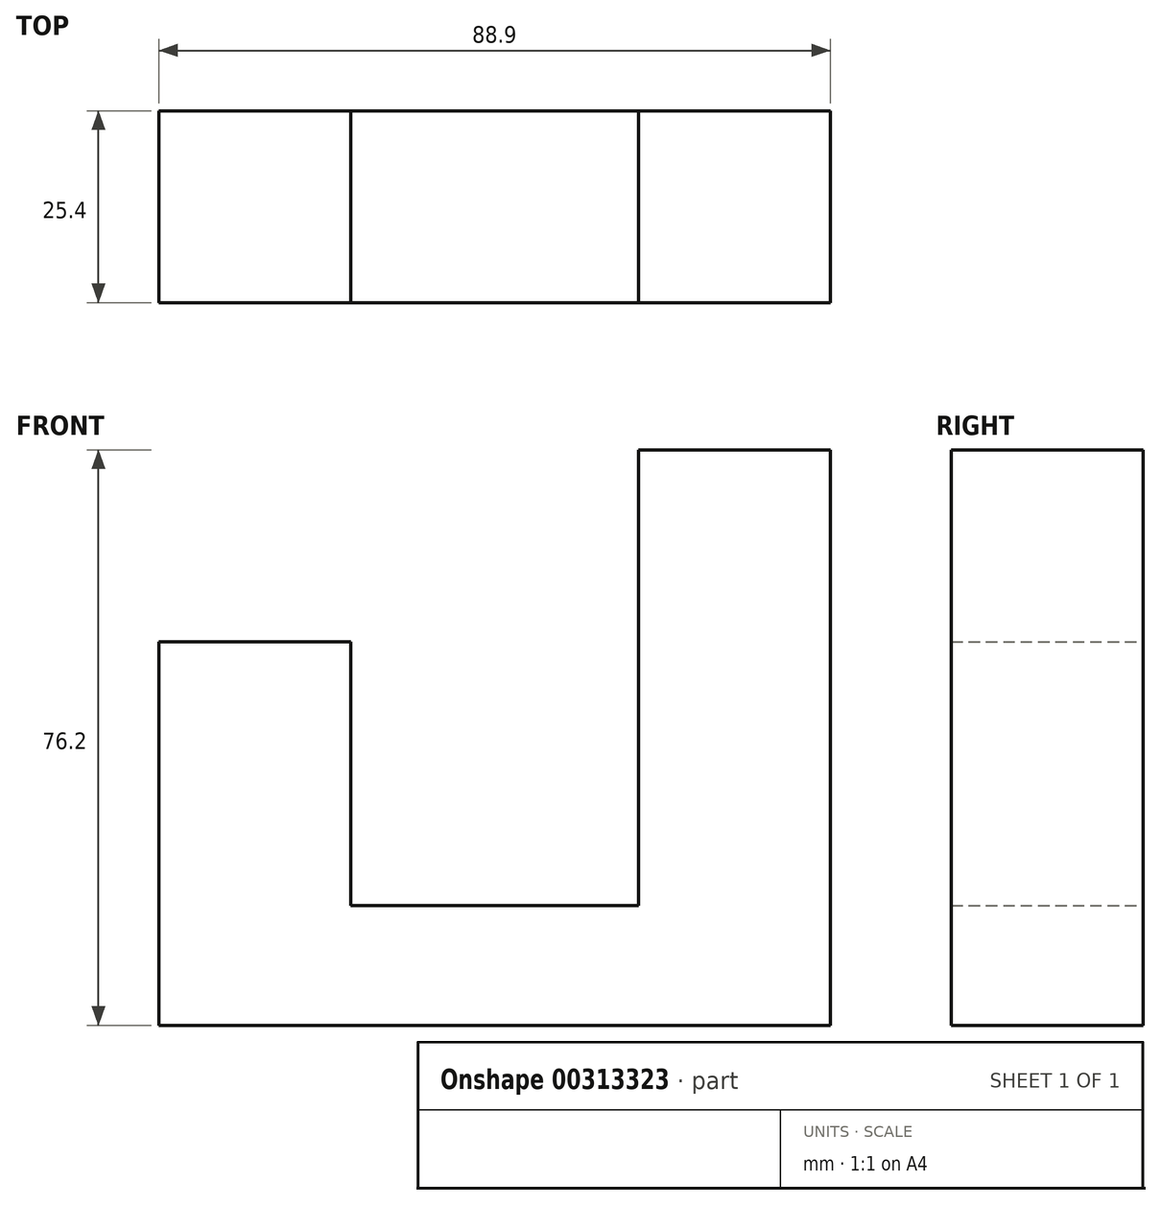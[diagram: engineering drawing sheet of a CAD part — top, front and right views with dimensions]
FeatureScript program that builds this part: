
annotation { "Feature Type Name" : "Feature", "Feature Type Description" : "" }
export const myFeature = defineFeature(function(context is Context, id is Id, definition is map)
    precondition{}
    {
        {
            var Q0;
            Q0=qCreatedBy(makeId("Front.planeOp"),FACE);
            var sketch = newSketch(context, id + "F0", { "sketchPlane" : qUnion([Q0])});
            skLineSegment(sketch, "E0", {"start": v(-58.85, 21.4) * mm, "end": v(-58.85, -29.4) * mm});
            skLineSegment(sketch, "E1", {"start": v(-58.85, -29.4) * mm, "end": v(30.05, -29.4) * mm});
            skLineSegment(sketch, "E2", {"start": v(30.05, -29.4) * mm, "end": v(30.05, 46.8) * mm});
            skLineSegment(sketch, "E3", {"start": v(30.05, 46.8) * mm, "end": v(4.65, 46.8) * mm});
            skLineSegment(sketch, "E4", {"start": v(4.65, 46.8) * mm, "end": v(4.65, -13.57) * mm});
            skLineSegment(sketch, "E5", {"start": v(4.65, -13.57) * mm, "end": v(-33.45, -13.57) * mm});
            skLineSegment(sketch, "E6", {"start": v(-33.45, -13.57) * mm, "end": v(-33.45, 21.4) * mm});
            skLineSegment(sketch, "E7", {"start": v(-58.85, 21.4) * mm, "end": v(-33.45, 21.4) * mm});
            skSolve(sketch);
        }
        {
            var Q0;
            Q0=makeQuery(id+"F0.imprint","IMPRINT",FACE,{"disambiguationData":[TD([[makeQuery(id+"F0.imprint","IMPRINT",EDGE,{"derivedFrom":sQuery(id+"F0.wireOp",EDGE,"E0")}),1.0]])]});
            extrude(context, id + "F1", {"entities" : qUnion([Q0]), "depth" : 25.4 * mm});
        }
    });
